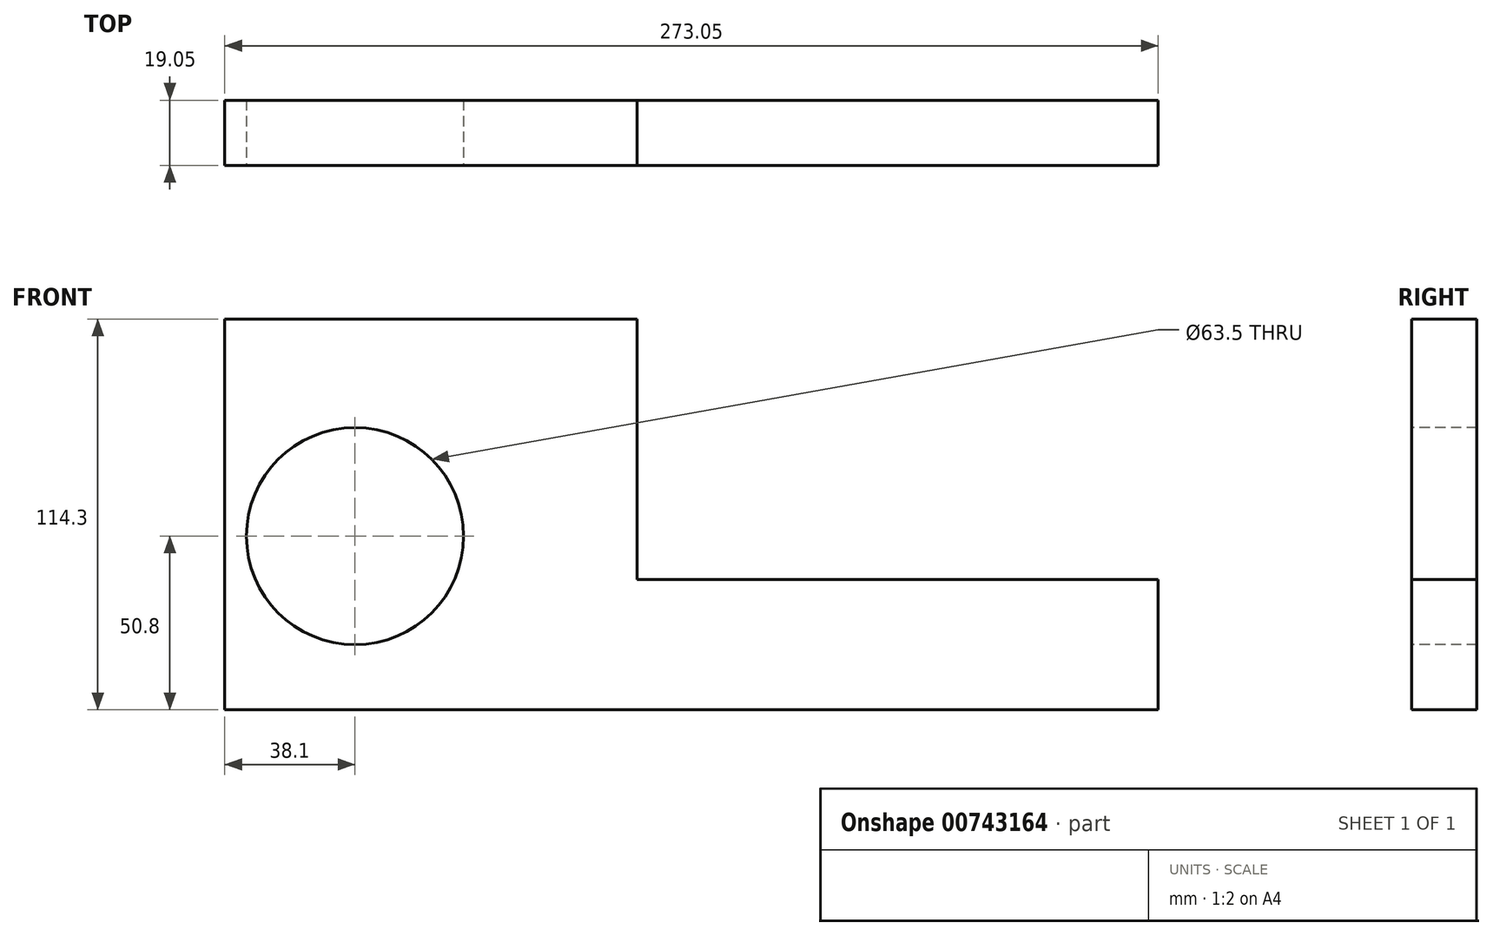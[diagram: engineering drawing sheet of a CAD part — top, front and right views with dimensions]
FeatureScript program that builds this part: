
annotation { "Feature Type Name" : "Feature", "Feature Type Description" : "" }
export const myFeature = defineFeature(function(context is Context, id is Id, definition is map)
    precondition{}
    {
        {
            var Q0;
            Q0=qCreatedBy(makeId("Front.planeOp"),FACE);
            var sketch = newSketch(context, id + "F0", { "sketchPlane" : qUnion([Q0])});
            skLineSegment(sketch, "E0.bottom", {"start": v(0, 0) * mm, "end": v(273.05, 0) * mm});
            skLineSegment(sketch, "E0.top", {"start": v(0, 114.3) * mm, "end": v(273.05, 114.3) * mm});
            skLineSegment(sketch, "E0.left", {"start": v(0, 0) * mm, "end": v(0, 114.3) * mm});
            skLineSegment(sketch, "E0.right", {"start": v(273.05, 0) * mm, "end": v(273.05, 114.3) * mm});
            skSolve(sketch);
        }
        {
            var Q0;
            Q0=qSketchRegion(id+"F0",true);
            extrude(context, id + "F1", {"entities" : qUnion([Q0]), "depth" : 19.05 * mm, "offsetDistance" : 25.4 * mm});
        }
        {
            var Q0;
            Q0=makeQuery(id+"F1.opExtrude","CAP_FACE",FACE,{"disambiguationData":[OSD([sQuery(id+"F0.wireOp",EDGE,"E0.bottom"),sQuery(id+"F0.wireOp",EDGE,"E0.top"),sQuery(id+"F0.wireOp",EDGE,"E0.left"),sQuery(id+"F0.wireOp",EDGE,"E0.right")])],"isStart":false});
            var sketch = newSketch(context, id + "F2", { "sketchPlane" : qUnion([Q0])});
            skCircle(sketch, "E1", {"center": v(38.1, 50.8) * mm, "radius": 31.75 * mm});
            skSolve(sketch);
        }
        {
            var Q0;
            Q0=makeQuery(id+"F2.imprint","IMPRINT",FACE,{"disambiguationData":[TD([[makeQuery(id+"F2.imprint","IMPRINT",EDGE,{"derivedFrom":sQuery(id+"F2.wireOp",EDGE,"E1")}),1.0]])]});
            extrude(context, id + "F3", {"entities" : qUnion([Q0]), "operationType" : NewBodyOperationType.REMOVE, "oppositeDirection" : true, "depth" : 25.4 * mm, "offsetDistance" : 25.4 * mm});
        }
        {
            var Q0;
            Q0=makeQuery(id+"F1.opExtrude","CAP_FACE",FACE,{"disambiguationData":[OSD([sQuery(id+"F0.wireOp",EDGE,"E0.bottom"),sQuery(id+"F0.wireOp",EDGE,"E0.top"),sQuery(id+"F0.wireOp",EDGE,"E0.left"),sQuery(id+"F0.wireOp",EDGE,"E0.right")])],"isStart":false});
            var sketch = newSketch(context, id + "F4", { "sketchPlane" : qUnion([Q0])});
            skLineSegment(sketch, "E2", {"start": v(273.05, 38.1) * mm, "end": v(120.65, 38.1) * mm});
            skLineSegment(sketch, "E3", {"start": v(120.65, 38.1) * mm, "end": v(120.65, 114.3) * mm});
            skLineSegment(sketch, "E4", {"start": v(120.65, 114.3) * mm, "end": v(273.05, 114.3) * mm});
            skLineSegment(sketch, "E5", {"start": v(273.05, 114.3) * mm, "end": v(273.05, 38.1) * mm});
            skSolve(sketch);
        }
        {
            var Q0;
            Q0=makeQuery(id+"F4.imprint","IMPRINT",FACE,{"disambiguationData":[TD([[makeQuery(id+"F4.imprint","IMPRINT",EDGE,{"derivedFrom":sQuery(id+"F4.wireOp",EDGE,"E2")}),-1.0]])]});
            extrude(context, id + "F5", {"entities" : qUnion([Q0]), "operationType" : NewBodyOperationType.REMOVE, "oppositeDirection" : true, "depth" : 25.4 * mm, "offsetDistance" : 25.4 * mm});
        }
    });
